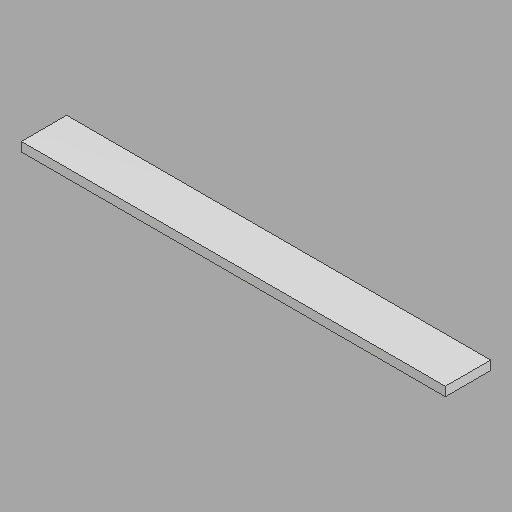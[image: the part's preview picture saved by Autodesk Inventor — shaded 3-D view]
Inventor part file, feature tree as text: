
AUTODESK INVENTOR PART (.ipt)
format: ipt  version: 2022.2 (Build 262287010, 287A)  size: 112,128 bytes
history: native  units: in
note: dims shown in document units (in); Inventor stores cm internally (conversion verified against a paired STEP export)
features: direct_edit x1, other x1, revolve x1
ambient origin geometry x8: Origin, YZ Plane, XZ Plane, XY Plane, X Axis, Y Axis, Z Axis, Center Point
bodies: Solid1 (feature_tree)
feature tree (3):
  direct_edit  "Direct Edit1"
  other  "R Vert rect jamb upper (3)"
  revolve  "Rotate1"  [1 undecoded]
note: 1 required parameter value undecoded (feature->parameter linkage not recoverable at this tier; creation-order binding heuristic only, values carry confidence <= 0.55)
